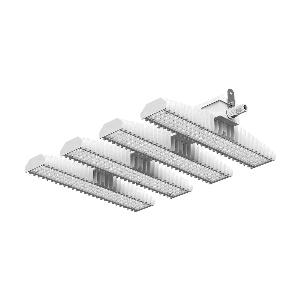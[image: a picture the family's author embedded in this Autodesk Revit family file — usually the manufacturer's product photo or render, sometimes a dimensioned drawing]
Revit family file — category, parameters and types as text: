
# Revit family: 3f_filippi_-_3f_lem_medio_3f_filippi_-_58913_-_3f_lem_4_led_200_dali_cr_medio
name_source: partatom
category: Lighting Fixtures
units: mm (PartAtom-declared; Revit-internal decimal feet)

## family parameters
Cut with Voids When Loaded = No
Host = Face
Light Source = No
Part Type = Normal
Room Calculation Point = No
Round Connector Dimension = Use Diameter
Shared = No

## types (1)
- 3F Filippi - 3F LEM Medio (1 x LED, 33259 lm, 218 W, 4000 K)
    Apparent Load = 218 VA
    Approval mark = CE
    CIE Flux Codes = 83 96 99 100 100
    Color Rendering = 80
    Color Temperature = 4000 K
    Control Gear = Electronic transformer
    Default Elevation = 1800 mm
    Description = Industrial luminaire with high light output and high luminous efficiency designed with the most innovative technologies for environments with temperature up to 55°C.

ILLUMINOTECHNICAL
Luminous efficiency 100% (DLOR 100%, ULOR 0%).
Initial luminous flux of the luminaire 33259 lm.
Medium distribution with rectangular shape.
Installation Interdistance Transv.D = 1.02 x hu - Long.D = 1.06 x hu.
Tabular UGR (CIE 117 - 4H-8H; S=0.25H; 70/50/20): RUG 19.2 - 18.8.
Beam angle: 65° - 67°.
Luminous efficacy 153 lm/W.
Lifetime (L93/B10): 30000 h. (tq+25°C)
Lifetime (L90/B10): 50000 h. (tq+25°C)
Lifetime (L85/B10): 80000 h. (tq+25°C)
Lifetime (L80/B10): 100000 h. (tq+25°C)
Lifetime (L85/B10): 50000 h. (tq+55°C)
Sudden decreased luminous flux after 50000 hours: 0% (C0).
Photobiological safety in compliance with IEC/TR 62778: RG0 risk exempt, (IEC 62471).
In compliance with IEC/EN 62722-2-1 - IEC/EN 62717 standards.

SOURCE
4 Mid-Power linear LED modules 50W/840.
Energy efficiency class (UE 2019/2020 - UE 2019/2015): C.
CIE 13.3 Colour rendering index: CRI >80 (R9 <50%).
IES TM-30 Fidelity Index: Rf = 84 Rg = 95.
CCT nominal colour temperature 4000 K.
Colour initial tolerance (MacAdam): SDCM 3.

MECHANICAL
Passive modular heatsinks in die-casted aluminium, painted in white colour.
To optimize the thermal management of the LED module, the heatsinks are oversized and provided with self-cleaning of cooling fins.
Wiring body in aluminium and galvanised steel anchored solidly to the sinks and thermally separated.
3F Lens lenses with high luminous efficiency, transparent methacrylate (PMMA), fixed to the LED modules.
Fixing brackets in stainless steel.
Luminaire with limited surface temperature. - D - (EN 60598-2-24)
Dimensions: 757x542 mm, height 129 mm. Weight 16.99 kg.
IP65 protection degree.
Mechanical strength to impacts IK06 (1 joule).
Glow-wire test resistance 650°C.

ELECTRICAL
Halogen Free DALI-2 DATI (Parts 251, 252, 253), PUSH-DIM, electronic wiring 230V-50/60Hz, power factor 0.97 at full load, THD <25%, constant output current, class I, 2 driver, 2 DALI addresses.
Power of the luminaire 218 W.
ENEC - CE.
Flicker: <4%.
Luminaire compliant with EN 60598-2-22 for power supply from a centralised emergency system CPSS (Central Power Supply System), not incorporated in the luminaire - high risk areas excluded. The default power and flux are 100% in AC and 15% in DC.
Ambient temperature from -30°C to +55°C.
Temperature class T6 max 85°C.
Quick connection via M25 5P connector with 9-13 mm tightening range.
Power unit positioned on a separate compartment by the LED module to ensure optimum temperatures of cabling components, to be inspectable and maintainable.
Relative humidity UR: <85%.

INSTALLATION
Ceiling / Suspended / Wall.
All accessories dedicated to this product are available on the Catalog and on our website www.3F-Filippi.com.

APPLICATIONS
In commercial environments, exhibition and industrial areas, stores, open areas.
Applications with high ambient temperature up to 55°C.
Environments in which it is necessary a total protection against falling fragments (eg environments with foodstuffs or machines with moving parts or with extreme temperature changes), use luminaires with polycarbonate lenses.

LIGHT MANAGEMENT
Recommended minimum setting: 10%.
The luminaire, equipped with (DALI-2 DATI) driver, can be controlled manually with 3F Easy Dim technology or automatically/manually with wired or wireless DALI/D2D control systems.
The D2D driver guarantees interoperability with other devices with the same certification by making the following information available:
Device Data (Part 251), Energy Report (Part 252), Diagnosis & Maintenance (Part 253).
In electrical systems without a regulation system (manual or automatic) and DALI bus, a suitable jumper must be made on the DA-DA terminals of the appliance.

WARNING
Fixture not suitable for cold stores with an ambient temperature <0°C and/or relative humidity >85%.
Luminaire designed for disposal/recycling at end-of-life.
Replaceable (LED only) light source by a professional. Replaceable control gear by a professional.
    Height = 129 mm
    Lamp = 1 x LED
    Lamp Light Flux = 33259 lm
    Lamp Power = 218 W
    Lamp count = 1
    Length = 757 mm
    Lifetime = 50000 h
    Luminous efficacy = 153 lm/W
    Manufacturer = 3F Filippi
    ModVariant = No
    Model = 3F Filippi - 58913 - 3F LEM 4 LED 200 DALI CR MEDIO
    Mounting Place = Ceiling
    Mounting Type = Pendant
    Number of Poles = 1
    OnlyDefault = Yes
    Power Factor = 1
    Product Name = 3F Filippi - 3F LEM Medio
    Product group = pendant luminaire
    ProductGroupID = 9
    Protection Class = Protection class I
    Protection Degree = IP 65
    RLX_Detail_Level = 1
    RLX_Emergency_Light_Flux = 0 lm
    RLX_Emergency_Type = 0
    RLX_Emergency_Type_DB = No
    RlxData = <blob elided: 118093 chars, md5=9bf4fccc>
    Socket = socket
    Standby Power = 0 W
    System Light Flux = 33259 lm
    System Power = 218 W
    Type Comments = Product without accessories
    Type Image = 3f_filippi_-_lem_4.jpg
    URL = http://relux.com
    VarID = ---
    Voltage = 0 V
    Weight = 0.00 kg
    Width = 542 mm

## geometry (parser evidence)
native form markers: Blend x4, Sweep x13
no freeform markers — native parametric forms only
